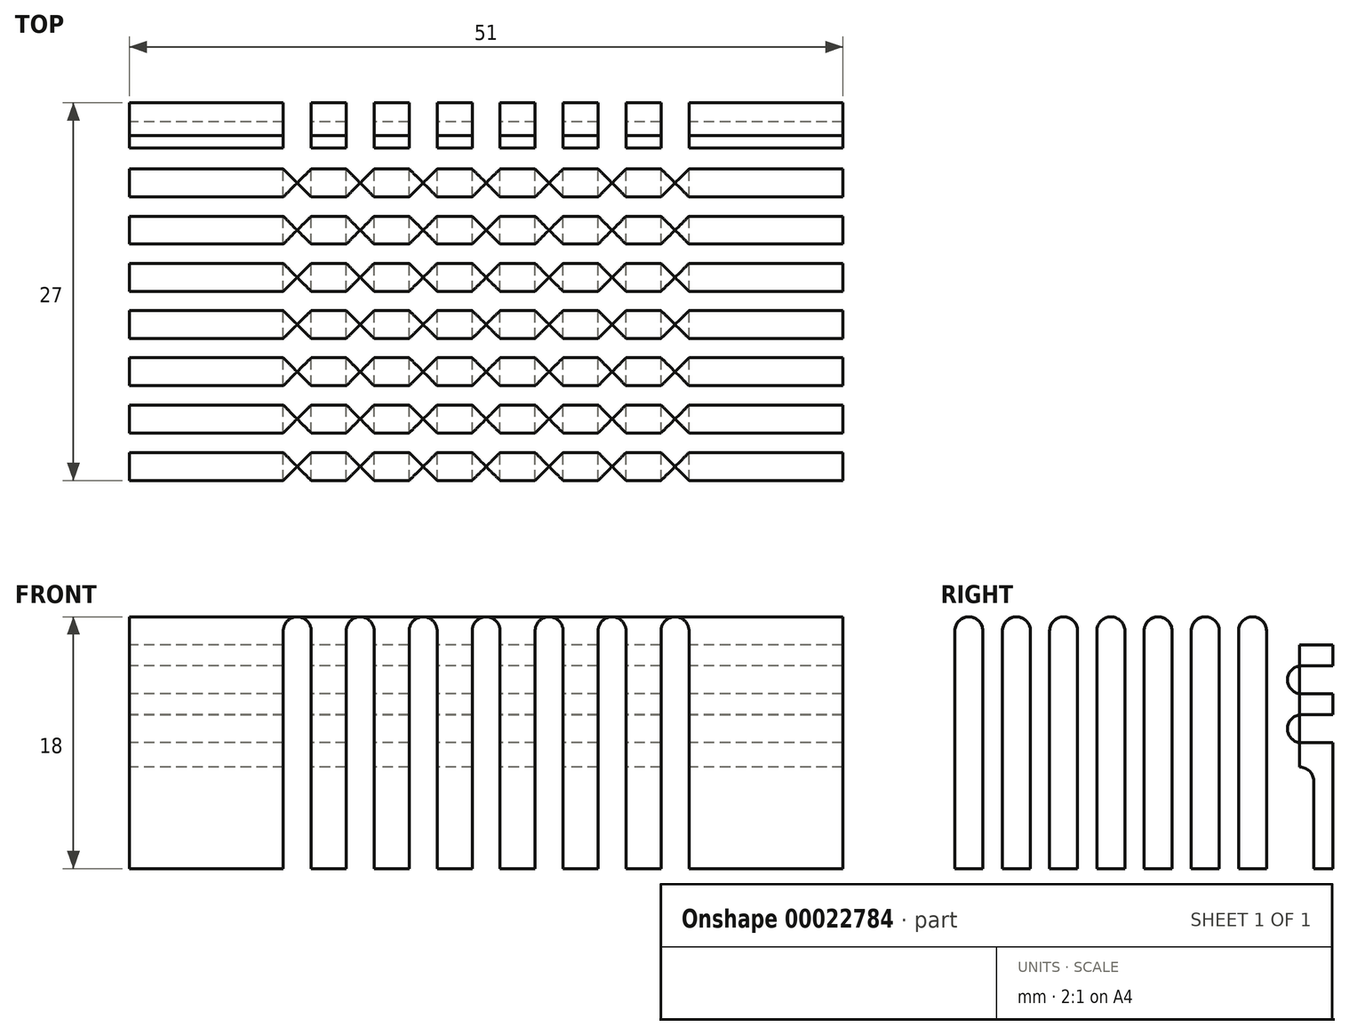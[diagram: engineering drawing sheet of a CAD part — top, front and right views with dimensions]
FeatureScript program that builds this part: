
annotation { "Feature Type Name" : "Feature", "Feature Type Description" : "" }
export const myFeature = defineFeature(function(context is Context, id is Id, definition is map)
    precondition{}
    {
        {
            var Q0;
            Q0=qCreatedBy(makeId("Top.planeOp"),FACE);
            var sketch = newSketch(context, id + "F0", { "sketchPlane" : qUnion([Q0])});
            skLineSegment(sketch, "E0.bottom", {"start": v(-25.5, 26) * mm, "end": v(25.5, 26) * mm});
            skLineSegment(sketch, "E0.top", {"start": v(-25.5, -26) * mm, "end": v(25.5, -26) * mm});
            skLineSegment(sketch, "E0.left", {"start": v(-25.5, 26) * mm, "end": v(-25.5, -26) * mm});
            skLineSegment(sketch, "E0.right", {"start": v(25.5, 26) * mm, "end": v(25.5, -26) * mm});
            skPoint(sketch, "E0.middle", {"position": v(0, 0) * mm});
            skSolve(sketch);
        }
        {
            var Q0;
            Q0 = qSketchRegion(id + "F0", true);
            extrude(context, id + "F1", {"entities" : qUnion([Q0]), "depth" : 20 * mm});
        }
        {
            var Q0;
            Q0=makeQuery(id+"F1.opExtrude","SWEPT_FACE",FACE,{"disambiguationData":[OSD([sQuery(id+"F0.wireOp",EDGE,"E0.left")])]});
            var sketch = newSketch(context, id + "F2", { "sketchPlane" : qUnion([Q0])});
            skLineSegment(sketch, "E1.0", {"start": v(-26, 20) * mm, "end": v(26, 20) * mm});
            skLineSegment(sketch, "E2.0", {"start": v(-26, 20) * mm, "end": v(-26, 0) * mm});
            skLineSegment(sketch, "E3.0", {"start": v(-26, 0) * mm, "end": v(26, 0) * mm});
            skLineSegment(sketch, "E3.1", {"start": v(26, 20) * mm, "end": v(26, 0) * mm});
            skLineSegment(sketch, "E4", {"start": v(-26, 17) * mm, "end": v(-23.77, 17) * mm});
            skLineSegment(sketch, "E5.0.1.0", {"start": v(-26, 13.5) * mm, "end": v(-23.77, 13.5) * mm});
            skLineSegment(sketch, "E5.0.2.0", {"start": v(-26, 10) * mm, "end": v(-23.77, 10) * mm});
            skLineSegment(sketch, "E5.direction1", {"start": v(-26, 17) * mm, "end": v(-20.95, 17) * mm, "construction": true});
            skLineSegment(sketch, "E5.direction2", {"start": v(-26, 17) * mm, "end": v(-26, 13.5) * mm, "construction": true});
            skArc(sketch, "E6.0.startCap", {"start": v(-26, 16) * mm, "mid": v(-27, 17) * mm, "end": v(-26, 18) * mm});
            skArc(sketch, "E6.0.endCap", {"start": v(-23.77, 18) * mm, "mid": v(-22.77, 17) * mm, "end": v(-23.77, 16) * mm});
            skLineSegment(sketch, "E6.0.left", {"start": v(-26, 18) * mm, "end": v(-23.77, 18) * mm});
            skLineSegment(sketch, "E6.0.right", {"start": v(-26, 16) * mm, "end": v(-23.77, 16) * mm});
            skArc(sketch, "E6.1.startCap", {"start": v(-26, 12.5) * mm, "mid": v(-27, 13.5) * mm, "end": v(-26, 14.5) * mm});
            skArc(sketch, "E6.1.endCap", {"start": v(-23.77, 14.5) * mm, "mid": v(-22.77, 13.5) * mm, "end": v(-23.77, 12.5) * mm});
            skLineSegment(sketch, "E6.1.left", {"start": v(-26, 14.5) * mm, "end": v(-23.77, 14.5) * mm});
            skLineSegment(sketch, "E6.1.right", {"start": v(-26, 12.5) * mm, "end": v(-23.77, 12.5) * mm});
            skArc(sketch, "E6.2.startCap", {"start": v(-26, 9) * mm, "mid": v(-27, 10) * mm, "end": v(-26, 11) * mm});
            skArc(sketch, "E6.2.endCap", {"start": v(-23.77, 11) * mm, "mid": v(-22.77, 10) * mm, "end": v(-23.77, 9) * mm});
            skLineSegment(sketch, "E6.2.left", {"start": v(-26, 11) * mm, "end": v(-23.77, 11) * mm});
            skLineSegment(sketch, "E6.2.right", {"start": v(-26, 9) * mm, "end": v(-23.77, 9) * mm});
            skLineSegment(sketch, "E7", {"start": v(0, 0) * mm, "end": v(0, 17) * mm});
            skPoint(sketch, "E7.endSnap0", {"position": v(-22.77, 17) * mm});
            skLineSegment(sketch, "E8", {"start": v(-3.4, 0) * mm, "end": v(-3.4, 17) * mm});
            skLineSegment(sketch, "E9.1.0.0", {"start": v(-6.77, 0) * mm, "end": v(-6.77, 17) * mm});
            skLineSegment(sketch, "E9.2.0.0", {"start": v(-10.15, 0) * mm, "end": v(-10.15, 17) * mm});
            skLineSegment(sketch, "E9.3.0.0", {"start": v(-13.52, 0) * mm, "end": v(-13.52, 17) * mm});
            skLineSegment(sketch, "E9.4.0.0", {"start": v(-16.9, 0) * mm, "end": v(-16.9, 17) * mm});
            skLineSegment(sketch, "E9.5.0.0", {"start": v(-20.27, 0) * mm, "end": v(-20.27, 17) * mm});
            skLineSegment(sketch, "E9.6.0.0", {"start": v(-23.65, 0) * mm, "end": v(-23.65, 6.26) * mm});
            skLineSegment(sketch, "E9.direction1", {"start": v(-3.5, 0) * mm, "end": v(-6.9, 0) * mm, "construction": true});
            skLineSegment(sketch, "E10", {"start": v(-23.65, 6.26) * mm, "end": v(-23.65, 17) * mm});
            skArc(sketch, "E11.0.startCap", {"start": v(1, 0) * mm, "mid": v(0, -1) * mm, "end": v(-1, 0) * mm});
            skArc(sketch, "E11.0.endCap", {"start": v(-1, 17) * mm, "mid": v(0, 18) * mm, "end": v(1, 17) * mm});
            skLineSegment(sketch, "E11.0.left", {"start": v(-1, 0) * mm, "end": v(-1, 17) * mm});
            skLineSegment(sketch, "E11.0.right", {"start": v(1, 0) * mm, "end": v(1, 17) * mm});
            skArc(sketch, "E11.1.startCap", {"start": v(-2.4, 0) * mm, "mid": v(-3.4, -1) * mm, "end": v(-4.4, 0) * mm});
            skArc(sketch, "E11.1.endCap", {"start": v(-4.4, 17) * mm, "mid": v(-3.4, 18) * mm, "end": v(-2.4, 17) * mm});
            skLineSegment(sketch, "E11.1.left", {"start": v(-4.4, 0) * mm, "end": v(-4.4, 17) * mm});
            skLineSegment(sketch, "E11.1.right", {"start": v(-2.4, 0) * mm, "end": v(-2.4, 17) * mm});
            skArc(sketch, "E11.2.startCap", {"start": v(-5.77, 0) * mm, "mid": v(-6.77, -1) * mm, "end": v(-7.77, 0) * mm});
            skArc(sketch, "E11.2.endCap", {"start": v(-7.77, 17) * mm, "mid": v(-6.77, 18) * mm, "end": v(-5.77, 17) * mm});
            skLineSegment(sketch, "E11.2.left", {"start": v(-7.77, 0) * mm, "end": v(-7.77, 17) * mm});
            skLineSegment(sketch, "E11.2.right", {"start": v(-5.77, 0) * mm, "end": v(-5.77, 17) * mm});
            skArc(sketch, "E11.3.startCap", {"start": v(-9.15, 0) * mm, "mid": v(-10.15, -1) * mm, "end": v(-11.15, 0) * mm});
            skArc(sketch, "E11.3.endCap", {"start": v(-11.15, 17) * mm, "mid": v(-10.15, 18) * mm, "end": v(-9.15, 17) * mm});
            skLineSegment(sketch, "E11.3.left", {"start": v(-11.15, 0) * mm, "end": v(-11.15, 17) * mm});
            skLineSegment(sketch, "E11.3.right", {"start": v(-9.15, 0) * mm, "end": v(-9.15, 17) * mm});
            skArc(sketch, "E11.4.startCap", {"start": v(-12.52, 0) * mm, "mid": v(-13.52, -1) * mm, "end": v(-14.52, 0) * mm});
            skArc(sketch, "E11.4.endCap", {"start": v(-14.52, 17) * mm, "mid": v(-13.52, 18) * mm, "end": v(-12.52, 17) * mm});
            skLineSegment(sketch, "E11.4.left", {"start": v(-14.52, 0) * mm, "end": v(-14.52, 17) * mm});
            skLineSegment(sketch, "E11.4.right", {"start": v(-12.52, 0) * mm, "end": v(-12.52, 17) * mm});
            skArc(sketch, "E11.5.startCap", {"start": v(-15.9, 0) * mm, "mid": v(-16.9, -1) * mm, "end": v(-17.9, 0) * mm});
            skArc(sketch, "E11.5.endCap", {"start": v(-17.9, 17) * mm, "mid": v(-16.9, 18) * mm, "end": v(-15.9, 17) * mm});
            skLineSegment(sketch, "E11.5.left", {"start": v(-17.9, 0) * mm, "end": v(-17.9, 17) * mm});
            skLineSegment(sketch, "E11.5.right", {"start": v(-15.9, 0) * mm, "end": v(-15.9, 17) * mm});
            skArc(sketch, "E11.6.startCap", {"start": v(-19.27, 0) * mm, "mid": v(-20.27, -1) * mm, "end": v(-21.27, 0) * mm});
            skArc(sketch, "E11.6.endCap", {"start": v(-21.27, 17) * mm, "mid": v(-20.27, 18) * mm, "end": v(-19.27, 17) * mm});
            skLineSegment(sketch, "E11.6.left", {"start": v(-21.27, 0) * mm, "end": v(-21.27, 17) * mm});
            skLineSegment(sketch, "E11.6.right", {"start": v(-19.27, 0) * mm, "end": v(-19.27, 17) * mm});
            skArc(sketch, "E11.7.startCap", {"start": v(-22.65, 0) * mm, "mid": v(-23.65, -1) * mm, "end": v(-24.65, 0) * mm});
            skArc(sketch, "E11.7.endCap", {"start": v(-24.65, 6.26) * mm, "mid": v(-23.65, 7.26) * mm, "end": v(-22.65, 6.26) * mm});
            skLineSegment(sketch, "E11.7.left", {"start": v(-24.65, 0) * mm, "end": v(-24.65, 6.26) * mm});
            skLineSegment(sketch, "E11.7.right", {"start": v(-22.65, 0) * mm, "end": v(-22.65, 6.26) * mm});
            skLineSegment(sketch, "E12.MirrorCS", {"start": v(4.4, 0) * mm, "end": v(4.4, 17) * mm});
            skArc(sketch, "E13.MirrorCS", {"start": v(4.4, 17) * mm, "mid": v(3.4, 18) * mm, "end": v(2.4, 17) * mm});
            skLineSegment(sketch, "E14.MirrorCS", {"start": v(2.4, 0) * mm, "end": v(2.4, 17) * mm});
            skLineSegment(sketch, "E15.MirrorCS", {"start": v(5.77, 0) * mm, "end": v(5.77, 17) * mm});
            skArc(sketch, "E16.MirrorCS", {"start": v(7.77, 17) * mm, "mid": v(6.77, 18) * mm, "end": v(5.77, 17) * mm});
            skLineSegment(sketch, "E17.MirrorCS", {"start": v(7.77, 0) * mm, "end": v(7.77, 17) * mm});
            skArc(sketch, "E18.MirrorCS", {"start": v(11.15, 17) * mm, "mid": v(10.15, 18) * mm, "end": v(9.15, 17) * mm});
            skLineSegment(sketch, "E19.MirrorCS", {"start": v(9.15, 0) * mm, "end": v(9.15, 17) * mm});
            skLineSegment(sketch, "E20.MirrorCS", {"start": v(11.15, 0) * mm, "end": v(11.15, 17) * mm});
            skLineSegment(sketch, "E21.MirrorCS", {"start": v(12.52, 0) * mm, "end": v(12.52, 17) * mm});
            skArc(sketch, "E22.MirrorCS", {"start": v(14.52, 17) * mm, "mid": v(13.52, 18) * mm, "end": v(12.52, 17) * mm});
            skLineSegment(sketch, "E23.MirrorCS", {"start": v(14.52, 0) * mm, "end": v(14.52, 17) * mm});
            skLineSegment(sketch, "E24.MirrorCS", {"start": v(15.9, 0) * mm, "end": v(15.9, 17) * mm});
            skArc(sketch, "E25.MirrorCS", {"start": v(17.9, 17) * mm, "mid": v(16.9, 18) * mm, "end": v(15.9, 17) * mm});
            skLineSegment(sketch, "E26.MirrorCS", {"start": v(17.9, 0) * mm, "end": v(17.9, 17) * mm});
            skArc(sketch, "E27.MirrorCS", {"start": v(21.27, 17) * mm, "mid": v(20.27, 18) * mm, "end": v(19.27, 17) * mm});
            skLineSegment(sketch, "E28.MirrorCS", {"start": v(21.27, 0) * mm, "end": v(21.27, 17) * mm});
            skLineSegment(sketch, "E29.MirrorCS", {"start": v(19.27, 0) * mm, "end": v(19.27, 17) * mm});
            skLineSegment(sketch, "E30.MirrorCS", {"start": v(22.65, 0) * mm, "end": v(22.65, 6.26) * mm});
            skLineSegment(sketch, "E31.MirrorCS", {"start": v(24.65, 0) * mm, "end": v(24.65, 6.26) * mm});
            skArc(sketch, "E32.MirrorCS", {"start": v(24.65, 6.26) * mm, "mid": v(23.65, 7.26) * mm, "end": v(22.65, 6.26) * mm});
            skArc(sketch, "E33.MirrorCS", {"start": v(23.77, 11) * mm, "mid": v(22.77, 10) * mm, "end": v(23.77, 9) * mm});
            skArc(sketch, "E34.MirrorCS", {"start": v(23.77, 14.5) * mm, "mid": v(22.77, 13.5) * mm, "end": v(23.77, 12.5) * mm});
            skArc(sketch, "E35.MirrorCS", {"start": v(23.77, 18) * mm, "mid": v(22.77, 17) * mm, "end": v(23.77, 16) * mm});
            skLineSegment(sketch, "E36.MirrorCS", {"start": v(26, 18) * mm, "end": v(23.77, 18) * mm});
            skLineSegment(sketch, "E37.MirrorCS", {"start": v(26, 16) * mm, "end": v(23.77, 16) * mm});
            skLineSegment(sketch, "E38.MirrorCS", {"start": v(26, 14.5) * mm, "end": v(23.77, 14.5) * mm});
            skLineSegment(sketch, "E39.MirrorCS", {"start": v(26, 12.5) * mm, "end": v(23.77, 12.5) * mm});
            skLineSegment(sketch, "E40.MirrorCS", {"start": v(26, 11) * mm, "end": v(23.77, 11) * mm});
            skLineSegment(sketch, "E41.MirrorCS", {"start": v(26, 9) * mm, "end": v(23.77, 9) * mm});
            skSolve(sketch);
        }
        {
            var Q0;
            Q0=makeQuery(id+"F2.imprint","IMPRINT",FACE,{"disambiguationData":[TD([[makeQuery(id+"F2.imprint","IMPRINT",EDGE,{"derivedFrom":sQuery(id+"F2.wireOp",EDGE,"E35.MirrorCS")}),1.0]])]});
            var Q1;
            Q1=makeQuery(id+"F2.imprint","IMPRINT",FACE,{"disambiguationData":[TD([[makeQuery(id+"F2.imprint","IMPRINT",EDGE,{"derivedFrom":sQuery(id+"F2.wireOp",EDGE,"E34.MirrorCS")}),1.0]])]});
            var Q2;
            Q2=makeQuery(id+"F2.imprint","IMPRINT",FACE,{"disambiguationData":[TD([[makeQuery(id+"F2.imprint","IMPRINT",EDGE,{"derivedFrom":sQuery(id+"F2.wireOp",EDGE,"E33.MirrorCS")}),1.0]])]});
            var Q3;
            {var subQ0=sQuery(id+"F2.wireOp",EDGE,"E30.MirrorCS");Q3=makeQuery(id+"F2.imprint","IMPRINT",FACE,{"disambiguationData":[TD([[makeQuery(id+"F2.imprint","IMPRINT",EDGE,{"derivedFrom":subQ0}),-1.0]])]});}
            var Q4;
            Q4=makeQuery(id+"F2.imprint","IMPRINT",FACE,{"disambiguationData":[TD([[makeQuery(id+"F2.imprint","IMPRINT",EDGE,{"derivedFrom":sQuery(id+"F2.wireOp",EDGE,"E27.MirrorCS")}),1.0]])]});
            var Q5;
            {var subQ0=sQuery(id+"F2.wireOp",EDGE,"E24.MirrorCS");Q5=makeQuery(id+"F2.imprint","IMPRINT",FACE,{"disambiguationData":[TD([[makeQuery(id+"F2.imprint","IMPRINT",EDGE,{"derivedFrom":subQ0}),-1.0]])]});}
            var Q6;
            {var subQ0=sQuery(id+"F2.wireOp",EDGE,"E21.MirrorCS");Q6=makeQuery(id+"F2.imprint","IMPRINT",FACE,{"disambiguationData":[TD([[makeQuery(id+"F2.imprint","IMPRINT",EDGE,{"derivedFrom":subQ0}),-1.0]])]});}
            var Q7;
            Q7=makeQuery(id+"F2.imprint","IMPRINT",FACE,{"disambiguationData":[TD([[makeQuery(id+"F2.imprint","IMPRINT",EDGE,{"derivedFrom":sQuery(id+"F2.wireOp",EDGE,"E18.MirrorCS")}),1.0]])]});
            var Q8;
            {var subQ0=sQuery(id+"F2.wireOp",EDGE,"E15.MirrorCS");Q8=makeQuery(id+"F2.imprint","IMPRINT",FACE,{"disambiguationData":[TD([[makeQuery(id+"F2.imprint","IMPRINT",EDGE,{"derivedFrom":subQ0}),-1.0]])]});}
            var Q9;
            {var subQ0=sQuery(id+"F2.wireOp",EDGE,"E12.MirrorCS");Q9=makeQuery(id+"F2.imprint","IMPRINT",FACE,{"disambiguationData":[TD([[makeQuery(id+"F2.imprint","IMPRINT",EDGE,{"derivedFrom":subQ0}),1.0]])]});}
            var Q10;
            Q10=makeQuery(id+"F2.imprint","IMPRINT",FACE,{"disambiguationData":[TD([[makeQuery(id+"F2.imprint","IMPRINT",EDGE,{"derivedFrom":sQuery(id+"F2.wireOp",EDGE,"E11.0.endCap")}),-1.0]])]});
            var Q11;
            Q11=makeQuery(id+"F2.imprint","IMPRINT",FACE,{"disambiguationData":[TD([[makeQuery(id+"F2.imprint","IMPRINT",EDGE,{"derivedFrom":sQuery(id+"F2.wireOp",EDGE,"E11.1.endCap")}),-1.0]])]});
            var Q12;
            Q12=makeQuery(id+"F2.imprint","IMPRINT",FACE,{"disambiguationData":[TD([[makeQuery(id+"F2.imprint","IMPRINT",EDGE,{"derivedFrom":sQuery(id+"F2.wireOp",EDGE,"E11.2.endCap")}),-1.0]])]});
            var Q13;
            Q13=makeQuery(id+"F2.imprint","IMPRINT",FACE,{"disambiguationData":[TD([[makeQuery(id+"F2.imprint","IMPRINT",EDGE,{"derivedFrom":sQuery(id+"F2.wireOp",EDGE,"E11.3.endCap")}),-1.0]])]});
            var Q14;
            Q14=makeQuery(id+"F2.imprint","IMPRINT",FACE,{"disambiguationData":[TD([[makeQuery(id+"F2.imprint","IMPRINT",EDGE,{"derivedFrom":sQuery(id+"F2.wireOp",EDGE,"E11.4.endCap")}),-1.0]])]});
            var Q15;
            Q15=makeQuery(id+"F2.imprint","IMPRINT",FACE,{"disambiguationData":[TD([[makeQuery(id+"F2.imprint","IMPRINT",EDGE,{"derivedFrom":sQuery(id+"F2.wireOp",EDGE,"E11.5.endCap")}),-1.0]])]});
            var Q16;
            Q16=makeQuery(id+"F2.imprint","IMPRINT",FACE,{"disambiguationData":[TD([[makeQuery(id+"F2.imprint","IMPRINT",EDGE,{"derivedFrom":sQuery(id+"F2.wireOp",EDGE,"E11.6.endCap")}),-1.0]])]});
            var Q17;
            {var subQ4=sQuery(id+"F2.wireOp",EDGE,"E9.6.0.0");Q17=makeQuery(id+"F2.imprint","IMPRINT",FACE,{"disambiguationData":[TD([[makeQuery(id+"F2.imprint","IMPRINT",EDGE,{"derivedFrom":subQ4}),1.0]])]});}
            var Q18;
            {var subQ4=sQuery(id+"F2.wireOp",EDGE,"E9.6.0.0");Q18=makeQuery(id+"F2.imprint","IMPRINT",FACE,{"disambiguationData":[TD([[makeQuery(id+"F2.imprint","IMPRINT",EDGE,{"derivedFrom":subQ4}),-1.0]])]});}
            var Q19;
            {var subQ4=sQuery(id+"F2.wireOp",EDGE,"E6.2.left");Q19=makeQuery(id+"F2.imprint","IMPRINT",FACE,{"disambiguationData":[TD([[makeQuery(id+"F2.imprint","IMPRINT",EDGE,{"derivedFrom":subQ4}),-1.0]])]});}
            var Q20;
            {var subQ0=sQuery(id+"F2.wireOp",EDGE,"E10");var subQ1=sQuery(id+"F2.wireOp",EDGE,"E6.2.endCap");var subQ2=makeQuery(id+"F2.imprint","INTERSECT",VERTEX,{"disambiguationData":[OD(0.0)],"derivedFrom":[subQ1,subQ0]});Q20=makeQuery(id+"F2.imprint","IMPRINT",FACE,{"disambiguationData":[TD([[makeQuery(id+"F2.imprint","IMPRINT",EDGE,{"disambiguationData":[TD([[subQ2,-1.0]])],"derivedFrom":subQ1}),-1.0]])]});}
            var Q21;
            {var subQ0=sQuery(id+"F2.wireOp",EDGE,"E6.1.left");Q21=makeQuery(id+"F2.imprint","IMPRINT",FACE,{"disambiguationData":[TD([[makeQuery(id+"F2.imprint","IMPRINT",EDGE,{"derivedFrom":subQ0}),-1.0]])]});}
            var Q22;
            {var subQ0=sQuery(id+"F2.wireOp",EDGE,"E10");var subQ1=sQuery(id+"F2.wireOp",EDGE,"E6.1.endCap");var subQ2=makeQuery(id+"F2.imprint","INTERSECT",VERTEX,{"disambiguationData":[OD(0.0)],"derivedFrom":[subQ1,subQ0]});Q22=makeQuery(id+"F2.imprint","IMPRINT",FACE,{"disambiguationData":[TD([[makeQuery(id+"F2.imprint","IMPRINT",EDGE,{"disambiguationData":[TD([[subQ2,-1.0]])],"derivedFrom":subQ1}),-1.0]])]});}
            var Q23;
            {var subQ3=sQuery(id+"F2.wireOp",EDGE,"E6.0.left");Q23=makeQuery(id+"F2.imprint","IMPRINT",FACE,{"disambiguationData":[TD([[makeQuery(id+"F2.imprint","IMPRINT",EDGE,{"derivedFrom":subQ3}),-1.0]])]});}
            extrude(context, id + "F3", {"entities" : qUnion([Q0, Q1, Q2, Q3, Q4, Q5, Q6, Q7, Q8, Q9, Q10, Q11, Q12, Q13, Q14, Q15, Q16, Q17, Q18, Q19, Q20, Q21, Q22, Q23]), "operationType" : NewBodyOperationType.REMOVE, "endBound" : BoundingType.THROUGH_ALL, "oppositeDirection" : true, "depth" : 25 * mm});
        }
        {
            var Q0;
            {var subQ2=sQuery(id+"F0.wireOp",EDGE,"E0.bottom");Q0=makeQuery(id+"F3.boolean.opBoolean","SPLIT",FACE,{"disambiguationData":[TD([makeQuery(id+"F3.opExtrude","SWEPT_FACE",FACE,{"disambiguationData":[OSD([sQuery(id+"F2.wireOp",EDGE,"E6.2.right")])]})])],"derivedFrom":makeQuery(id+"F1.opExtrude","SWEPT_FACE",FACE,{"disambiguationData":[OSD([subQ2])]})});}
            var sketch = newSketch(context, id + "F4", { "sketchPlane" : qUnion([Q0])});
            skLineSegment(sketch, "E42", {"start": v(0, 0) * mm, "end": v(0, 17) * mm, "construction": true});
            skPoint(sketch, "E42.endSnap0", {"position": v(0, 9) * mm});
            skLineSegment(sketch, "E43.1.0.0", {"start": v(4.5, 0) * mm, "end": v(4.5, 17) * mm, "construction": true});
            skLineSegment(sketch, "E43.2.0.0", {"start": v(9, 0) * mm, "end": v(9, 17) * mm, "construction": true});
            skLineSegment(sketch, "E43.3.0.0", {"start": v(13.5, 0) * mm, "end": v(13.5, 17) * mm, "construction": true});
            skLineSegment(sketch, "E43.direction1", {"start": v(0, 0) * mm, "end": v(4.5, 0) * mm, "construction": true});
            skArc(sketch, "E44.0.startCap", {"start": v(1, 0) * mm, "mid": v(0, -1) * mm, "end": v(-1, 0) * mm});
            skArc(sketch, "E44.0.endCap", {"start": v(-1, 17) * mm, "mid": v(0, 18) * mm, "end": v(1, 17) * mm});
            skLineSegment(sketch, "E44.0.left", {"start": v(-1, 0) * mm, "end": v(-1, 17) * mm});
            skLineSegment(sketch, "E44.0.right", {"start": v(1, 0) * mm, "end": v(1, 17) * mm});
            skArc(sketch, "E44.1.startCap", {"start": v(5.5, 0) * mm, "mid": v(4.5, -1) * mm, "end": v(3.5, 0) * mm});
            skArc(sketch, "E44.1.endCap", {"start": v(3.5, 17) * mm, "mid": v(4.5, 18) * mm, "end": v(5.5, 17) * mm});
            skLineSegment(sketch, "E44.1.left", {"start": v(3.5, 0) * mm, "end": v(3.5, 17) * mm});
            skLineSegment(sketch, "E44.1.right", {"start": v(5.5, 0) * mm, "end": v(5.5, 17) * mm});
            skArc(sketch, "E44.2.startCap", {"start": v(10, 0) * mm, "mid": v(9, -1) * mm, "end": v(8, 0) * mm});
            skArc(sketch, "E44.2.endCap", {"start": v(8, 17) * mm, "mid": v(9, 18) * mm, "end": v(10, 17) * mm});
            skLineSegment(sketch, "E44.2.left", {"start": v(8, 0) * mm, "end": v(8, 17) * mm});
            skLineSegment(sketch, "E44.2.right", {"start": v(10, 0) * mm, "end": v(10, 17) * mm});
            skArc(sketch, "E44.3.startCap", {"start": v(14.5, 0) * mm, "mid": v(13.5, -1) * mm, "end": v(12.5, 0) * mm});
            skArc(sketch, "E44.3.endCap", {"start": v(12.5, 17) * mm, "mid": v(13.5, 18) * mm, "end": v(14.5, 17) * mm});
            skLineSegment(sketch, "E44.3.left", {"start": v(12.5, 0) * mm, "end": v(12.5, 17) * mm});
            skLineSegment(sketch, "E44.3.right", {"start": v(14.5, 0) * mm, "end": v(14.5, 17) * mm});
            skArc(sketch, "E45.MirrorCS", {"start": v(-3.5, 17) * mm, "mid": v(-4.5, 18) * mm, "end": v(-5.5, 17) * mm});
            skLineSegment(sketch, "E46.MirrorCS", {"start": v(-3.5, 0) * mm, "end": v(-3.5, 17) * mm});
            skLineSegment(sketch, "E47.MirrorCS", {"start": v(-5.5, 0) * mm, "end": v(-5.5, 17) * mm});
            skLineSegment(sketch, "E48.MirrorCS", {"start": v(-8, 0) * mm, "end": v(-8, 17) * mm});
            skArc(sketch, "E49.MirrorCS", {"start": v(-8, 17) * mm, "mid": v(-9, 18) * mm, "end": v(-10, 17) * mm});
            skLineSegment(sketch, "E50.MirrorCS", {"start": v(-10, 0) * mm, "end": v(-10, 17) * mm});
            skLineSegment(sketch, "E51.MirrorCS", {"start": v(-12.5, 0) * mm, "end": v(-12.5, 17) * mm});
            skArc(sketch, "E52.MirrorCS", {"start": v(-12.5, 17) * mm, "mid": v(-13.5, 18) * mm, "end": v(-14.5, 17) * mm});
            skLineSegment(sketch, "E53.MirrorCS", {"start": v(-14.5, 0) * mm, "end": v(-14.5, 17) * mm});
            skLineSegment(sketch, "E54.0", {"start": v(25.5, 0) * mm, "end": v(-25.5, 0) * mm});
            skSolve(sketch);
        }
        {
            var Q0;
            Q0 = qSketchRegion(id + "F4", true);
            extrude(context, id + "F5", {"entities" : qUnion([Q0]), "operationType" : NewBodyOperationType.REMOVE, "endBound" : BoundingType.THROUGH_ALL, "oppositeDirection" : true, "depth" : 25 * mm});
        }
    });
